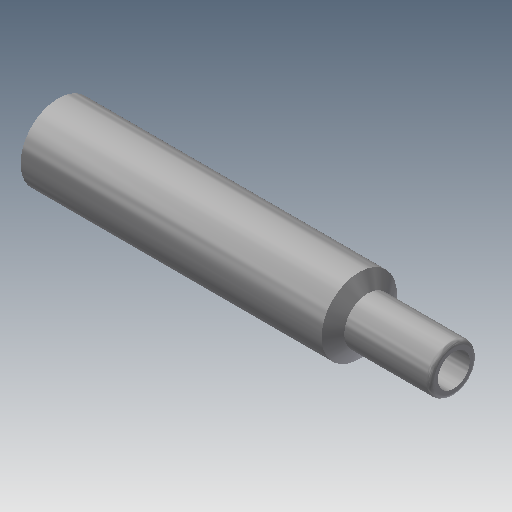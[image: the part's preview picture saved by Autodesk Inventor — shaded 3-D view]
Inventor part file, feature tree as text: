
AUTODESK INVENTOR PART (.ipt)
format: ipt  version: 2021 (Build 250183000, 183)  size: 144,896 bytes
history: native  units: mm
features: other x1, revolve x1, fillet x1, sketch x1
ambient origin geometry x8: Origin, YZ Plane, XZ Plane, XY Plane, X Axis, Y Axis, Z Axis, Center Point
bodies: Body1 (feature_tree)
feature tree (4):
  other  "Sólido2"
  revolve  "Revolución2"  [1 undecoded]
  fillet  "Empalme2"  [1 undecoded]
  sketch  "Boceto1"  dims[d5=140.0mm d9=40.0mm d10=90.0deg d11=2.0mm d13=17.526mm d14=14.0mm]
note: 2 required parameter values undecoded (feature->parameter linkage not recoverable at this tier; creation-order binding heuristic only, values carry confidence <= 0.55)